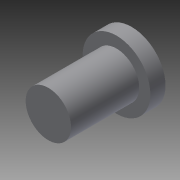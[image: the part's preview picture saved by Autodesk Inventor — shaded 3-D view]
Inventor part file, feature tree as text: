
AUTODESK INVENTOR PART (.ipt)
format: ipt  version: 2014 (Build 180170000, 170)  size: 81,408 bytes
history: native  units: mm
features: extrude x2, sketch x2
ambient origin geometry x8: Origin, YZ Plane, XZ Plane, XY Plane, X Axis, Y Axis, Z Axis, Center Point
bodies: Solid1 (feature_tree)
feature tree (4):
  extrude  "Extrusion1"  Depth=4.5mm TaperAngle=0.0deg
  extrude  "Extrusion2"  [1 undecoded]
  sketch  "Sketch1"  dims[d0=3.0mm d1=4.5mm d2=0.0mm]
  sketch  "Sketch2"  dims[d3=1.0mm d4=0.0mm]
note: 1 required parameter value undecoded (feature->parameter linkage not recoverable at this tier; creation-order binding heuristic only, values carry confidence <= 0.55)
